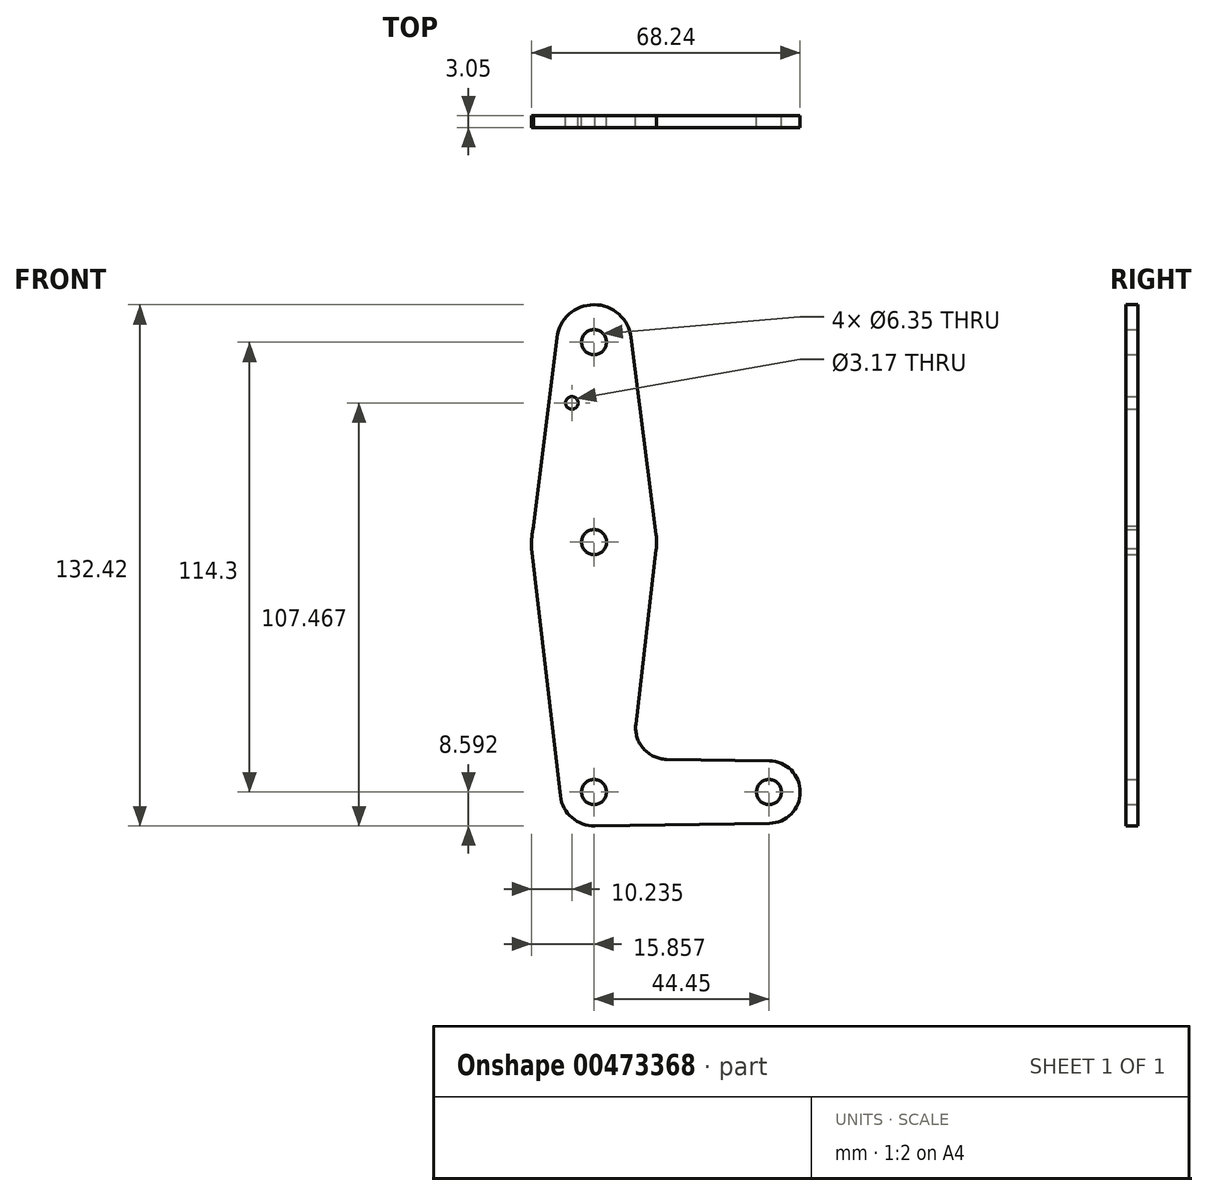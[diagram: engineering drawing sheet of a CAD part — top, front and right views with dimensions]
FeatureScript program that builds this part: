
annotation { "Feature Type Name" : "Feature", "Feature Type Description" : "" }
export const myFeature = defineFeature(function(context is Context, id is Id, definition is map)
    precondition{}
    {
        {
            var Q0;
            Q0=qCreatedBy(makeId("Front.planeOp"),FACE);
            var sketch = newSketch(context, id + "F0", { "sketchPlane" : qUnion([Q0])});
            skLineSegment(sketch, "E0", {"start": v(-24.54, -61.9) * mm, "end": v(19.9, -61.9) * mm, "construction": true});
            skCircle(sketch, "E1", {"center": v(-24.52, 1.6) * mm, "radius": 15.88 * mm});
            skCircle(sketch, "E2", {"center": v(-24.54, -61.9) * mm, "radius": 8.6 * mm});
            skCircle(sketch, "E3", {"center": v(19.9, -61.9) * mm, "radius": 7.94 * mm});
            skCircle(sketch, "E4", {"center": v(-24.54, 52.4) * mm, "radius": 9.53 * mm});
            skLineSegment(sketch, "E5", {"start": v(-24.54, 52.4) * mm, "end": v(-24.54, -61.9) * mm, "construction": true});
            skLineSegment(sketch, "E6", {"start": v(-34, 53.56) * mm, "end": v(-40.4, 1.4) * mm});
            skLineSegment(sketch, "E7", {"start": v(-40.4, 1.4) * mm, "end": v(-40.38, 0) * mm});
            skLineSegment(sketch, "E8", {"start": v(-40.38, 0) * mm, "end": v(-32.6, -67.09) * mm});
            skLineSegment(sketch, "E9", {"start": v(-15.1, 53.6) * mm, "end": v(-8.32, 0) * mm});
            skLineSegment(sketch, "E10", {"start": v(-8.75, -0.22) * mm, "end": v(-13.9, -44.71) * mm});
            skLineSegment(sketch, "E11", {"start": v(-6.12, -53.58) * mm, "end": v(20.02, -53.96) * mm});
            skLineSegment(sketch, "E12", {"start": v(-24.54, -70.5) * mm, "end": v(20.02, -69.83) * mm});
            skCircle(sketch, "E13", {"center": v(-24.54, 52.4) * mm, "radius": 3.18 * mm});
            skCircle(sketch, "E14", {"center": v(-24.52, 1.6) * mm, "radius": 3.18 * mm});
            skCircle(sketch, "E15", {"center": v(-24.54, -61.9) * mm, "radius": 3.18 * mm});
            skCircle(sketch, "E16", {"center": v(19.9, -61.9) * mm, "radius": 3.18 * mm});
            skCircle(sketch, "E17", {"center": v(-30.16, 36.98) * mm, "radius": 1.59 * mm});
            skPoint(sketch, "E18.newPointA", {"position": v(-16.5, -67.09) * mm});
            skPoint(sketch, "E18.newPointB", {"position": v(-24.54, -53.3) * mm});
            skArc(sketch, "E18.filletArc", {"start": v(-13.9, -44.71) * mm, "mid": v(-11.98, -50.87) * mm, "end": v(-6.12, -53.58) * mm});
            skSolve(sketch);
        }
        {
            var Q0;
            Q0 = qSketchRegion(id + "F0", true);
            extrude(context, id + "F1", {"entities" : qUnion([Q0]), "depth" : 3.05 * mm});
        }
    });
